# Revit family: Gira_5569920
name_source: partatom
category: Elektroinstallationen
revit_build: Autodesk Revit 2017 (Build: 20160225_1515(x64)
units: mm (PartAtom-declared; Revit-internal decimal feet)

## family parameters
Basisbauteil = Fläche
Beim Laden mit Abzugskörper schneiden = Nein
Bemaßung runder Anschluss = Durchmesser verwenden
Beschriftungsausrichtung beibehalten = Nein
Gemeinsam genutzt = Nein
Raumberechnungspunkt = Nein
Teiletyp = Normal

## types (1)
- Gira_5569920
    Anzahl der Klingeltasten = 1
    BIM = https://media.stage.bim.site
    Beschreibung = System 106 Türstationsmodul mit Inbetriebnahme-Taste  Edelstahl   Inbetriebnahme-Taste Das Gira System 106 ist ein Installationssystem aus Echtmetall in puristisch-edlem Design ohne Rahmen, basierend auf einem Grundmaß von 106,5 × 106,5 mm. Mit der modularen Türstation im Gira System 106 beginnt Gastlichkeit schon vor der Haustür. Von Ruftasten-, Sprach- und Kameramodul bis hin zum Info- und Blindmodul präsentieren sich alle Funktionen in einem stimmigen Gesamtbild. Im Dunkeln sorgen die hinterleuchteten Ruftasten mit Beschriftungsfeld für gute Lesbarkeit und eine ansprechende Erscheinung.  Individuell anpassbar durch modularen Aufbau Das System 106 kann in Ein-und Mehrfamilienhäusern, aber auch in Bürogebäuden, Industrieobjekten und Hotels eingesetzt werden. Der modulare Aufbau ermöglicht es, das System in Größe, Design und Funktionalität individuell an den jeweiligen Bedarf anzupassen. Erweiterungen und Änderungen sind durch Modulaustausch jederzeit einfach möglich. Selbst ein reiner Frontwechsel ist mit dem System möglich. Somit kann das Erscheinungsbild der Anlage auch nachträglich von z. B. Verkehrsweiß auf die Oberfläche Edelstahl geändert werden, ohne dabei die Elektronikeinheiten mit tauschen zu müssen.  Hochwertige Materialien Die Module sind rahmenlos mit Echtmaterial-Designfronten in zwei gebürsteten Edelstahlvarianten (V2A und V4A), eloxiertem Aluminium C-0 und einer verkehrsweiß (RAL 9016) lackierten Metalllegierung erhältlich: robuste Materialien, die für Langlebigkeit sorgen. Kamera- und Anzeigemodul (DIN 18040) verfügen über eine Schwarzglasabdeckung.  Einfache Installation und stufenweise Montage Das System kann parallel zum Baufortschritt in verschiedenen Stufen installiert werden. So ist es möglich, beim Rohbau zunächst nur den unteren Teil des Aufputz-Gehäuses zu montieren, Leitungen und Module können dann hinzugefügt werden, wenn sie gebraucht werden.  Individuelle Beschriftungsmöglichkeiten Ruftasten- und Info-Module können über den Gira Beschriftungsservice individuell laserbeschriftet werden.  Merkmale: - Kompaktes Sprachmodul mit integriertem Ruftaster für die Kommunikation zwischen innen und außen. - Ein hochwertiges Mikrofon und ein wetterfester Lautsprecher sorgen für gute Verständigung. - Spannungsversorgung über 2-Draht Bus. Zusätzlicher Anschluss für ZV (z. B. notwendig ab 3. Kameramodul). - Alle anderen System 106 Module (außer Sprachmodul) werden über das Türstationsmodul mit Spannung versorgt.  Hinweise : - Professionelle Beschriftung über den Gira Beschriftungsservice www.beschriftung.gira.de.
    Breite [m] = 0.1065
    Datenblatt = https://katalog.gira.de
    GTIN = 4010337022459
    HAN = 5569920
    Hersteller = Gira
    Höhe [m] = 0.1065
    Installationstechnik = Bus-System
    Produktseite = http://katalog.gira.de
    Typname = Türstationsmodul IBN-Taste System 106 Edelstahl
    URL = https://www.gira.de
    Vorgabe-Ansicht = 1219 mm

## geometry (parser evidence)
native form markers: Sweep x1
no freeform markers — native parametric forms only
